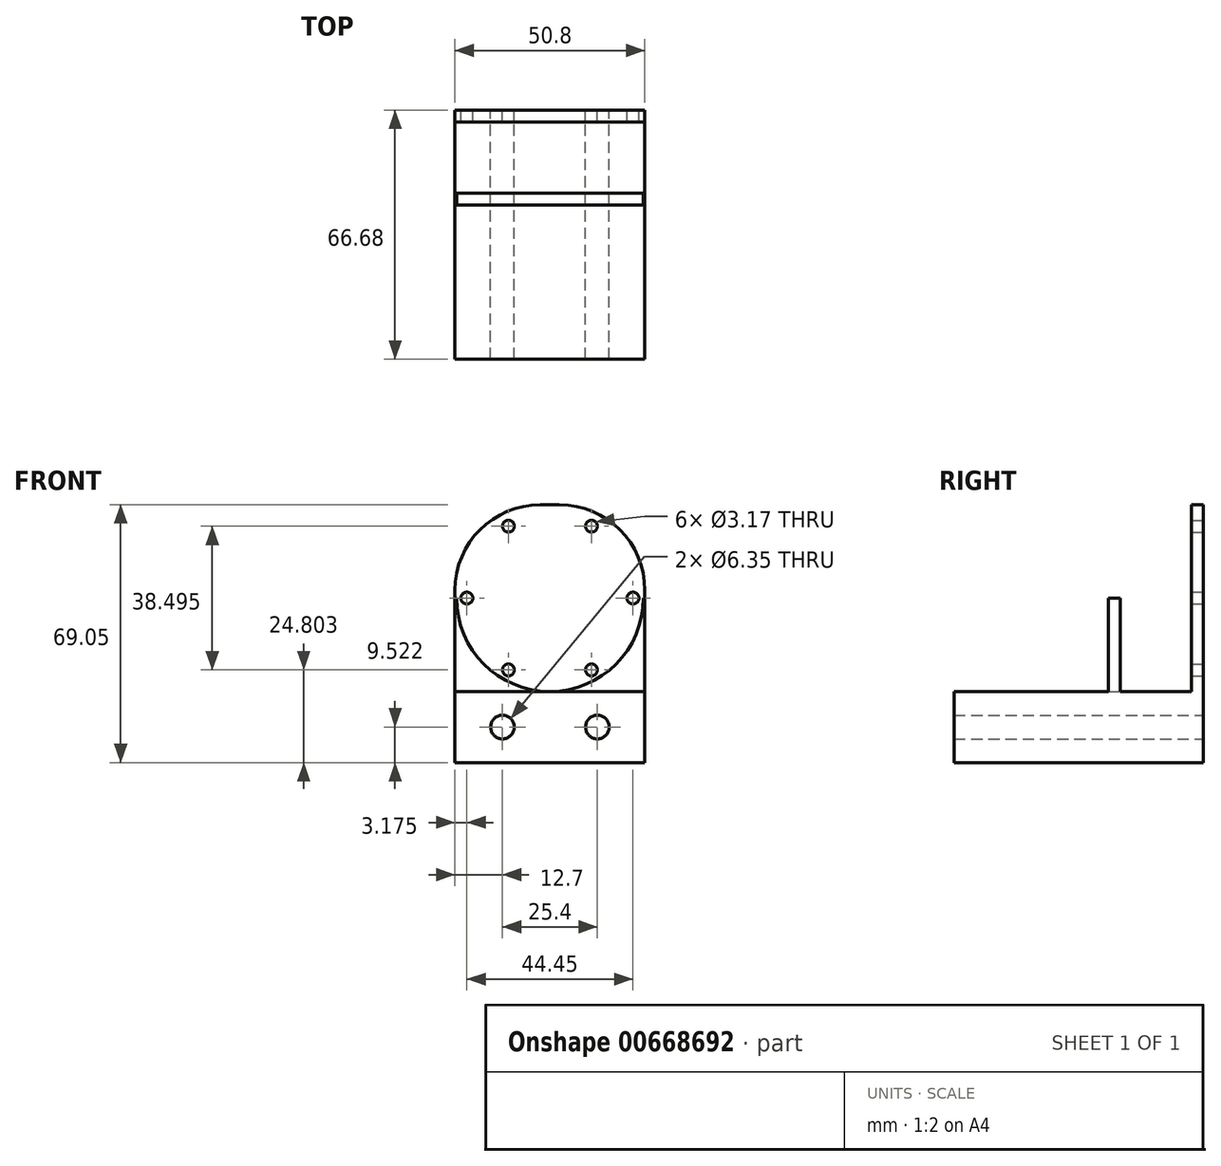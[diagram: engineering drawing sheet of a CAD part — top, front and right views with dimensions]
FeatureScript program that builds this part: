
annotation { "Feature Type Name" : "Feature", "Feature Type Description" : "" }
export const myFeature = defineFeature(function(context is Context, id is Id, definition is map)
    precondition{}
    {
        {
            var Q0;
            Q0=qCreatedBy(makeId("Front.planeOp"),FACE);
            var sketch = newSketch(context, id + "F0", { "sketchPlane" : qUnion([Q0])});
            skCircle(sketch, "E0", {"center": v(0, 0) * mm, "radius": 25 * mm});
            skCircle(sketch, "E1", {"center": v(0, 0) * mm, "radius": 23.81 * mm});
            skLineSegment(sketch, "E2", {"start": v(-23.81, 0) * mm, "end": v(-22.23, 0) * mm});
            skCircle(sketch, "E3", {"center": v(-22.23, 0) * mm, "radius": 1.59 * mm});
            skCircle(sketch, "E4.1.0", {"center": v(-11.11, -19.25) * mm, "radius": 1.59 * mm});
            skCircle(sketch, "E4.2.0", {"center": v(11.11, -19.25) * mm, "radius": 1.59 * mm});
            skCircle(sketch, "E4.3.0", {"center": v(22.23, 0) * mm, "radius": 1.59 * mm});
            skCircle(sketch, "E4.4.0", {"center": v(11.11, 19.25) * mm, "radius": 1.59 * mm});
            skCircle(sketch, "E4.5.0", {"center": v(-11.11, 19.25) * mm, "radius": 1.59 * mm});
            skLineSegment(sketch, "E5", {"start": v(0, -25) * mm, "end": v(-25.4, -25) * mm});
            skLineSegment(sketch, "E6", {"start": v(0, 25) * mm, "end": v(-25.4, 25) * mm});
            skLineSegment(sketch, "E7", {"start": v(-25.4, 25) * mm, "end": v(-25.4, -25) * mm});
            skLineSegment(sketch, "E8", {"start": v(0, -25) * mm, "end": v(25.4, -25) * mm});
            skLineSegment(sketch, "E9", {"start": v(0, 25) * mm, "end": v(25.4, 25) * mm});
            skLineSegment(sketch, "E10", {"start": v(25.4, 25) * mm, "end": v(25.4, -25) * mm});
            skLineSegment(sketch, "E11.bottom", {"start": v(-25.4, -25) * mm, "end": v(25.4, -25) * mm});
            skLineSegment(sketch, "E11.top", {"start": v(-25.4, -44.05) * mm, "end": v(25.4, -44.05) * mm});
            skLineSegment(sketch, "E11.left", {"start": v(-25.4, -25) * mm, "end": v(-25.4, -44.05) * mm});
            skLineSegment(sketch, "E11.right", {"start": v(25.4, -25) * mm, "end": v(25.4, -44.05) * mm});
            skLineSegment(sketch, "E12", {"start": v(-25.4, -34.53) * mm, "end": v(-12.7, -34.53) * mm});
            skCircle(sketch, "E13", {"center": v(-12.7, -34.53) * mm, "radius": 3.18 * mm});
            skCircle(sketch, "E14.MirrorC", {"center": v(12.7, -34.53) * mm, "radius": 3.18 * mm});
            skLineSegment(sketch, "E15", {"start": v(-23.81, 0) * mm, "end": v(-25.4, 0) * mm});
            skLineSegment(sketch, "E16", {"start": v(23.81, 0) * mm, "end": v(25.4, 0) * mm});
            skSolve(sketch);
        }
        {
            var Q0;
            {var subQ4=sQuery(id+"F0.wireOp",EDGE,"E11.top");Q0=makeQuery(id+"F0.imprint","IMPRINT",FACE,{"disambiguationData":[TD([[makeQuery(id+"F0.imprint","IMPRINT",EDGE,{"derivedFrom":subQ4}),1.0]])]});}
            extrude(context, id + "F1", {"entities" : qUnion([Q0]), "depth" : 66.67 * mm, "offsetDistance" : 25.4 * mm});
        }
        {
            var Q0;
            {var subQ0=sQuery(id+"F0.wireOp",EDGE,"E15");var subQ1=sQuery(id+"F0.wireOp",EDGE,"E0");var subQ2=makeQuery(id+"F0.imprint","INTERSECT",VERTEX,{"derivedFrom":[subQ1,subQ0]});Q0=makeQuery(id+"F0.imprint","IMPRINT",FACE,{"disambiguationData":[TD([[makeQuery(id+"F0.imprint","IMPRINT",EDGE,{"disambiguationData":[TD([[subQ2,-1.0]])],"derivedFrom":subQ1}),-1.0]])]});}
            var Q1;
            {var subQ0=sQuery(id+"F0.wireOp",EDGE,"E16");var subQ1=sQuery(id+"F0.wireOp",EDGE,"E0");var subQ2=makeQuery(id+"F0.imprint","INTERSECT",VERTEX,{"derivedFrom":[subQ1,subQ0]});Q1=makeQuery(id+"F0.imprint","IMPRINT",FACE,{"disambiguationData":[TD([[makeQuery(id+"F0.imprint","IMPRINT",EDGE,{"disambiguationData":[TD([[subQ2,1.0]])],"derivedFrom":subQ1}),-1.0]])]});}
            extrude(context, id + "F2", {"entities" : qUnion([Q0, Q1]), "operationType" : NewBodyOperationType.ADD, "depth" : 25.4 * mm, "offsetDistance" : 25.4 * mm});
        }
        {
            var Q0;
            {var subQ0=sQuery(id+"F0.wireOp",EDGE,"E15");var subQ1=sQuery(id+"F0.wireOp",EDGE,"E0");var subQ2=makeQuery(id+"F0.imprint","INTERSECT",VERTEX,{"derivedFrom":[subQ1,subQ0]});Q0=makeQuery(id+"F0.imprint","IMPRINT",FACE,{"disambiguationData":[TD([[makeQuery(id+"F0.imprint","IMPRINT",EDGE,{"disambiguationData":[TD([[subQ2,-1.0]])],"derivedFrom":subQ1}),-1.0]])]});}
            var Q1;
            {var subQ0=sQuery(id+"F0.wireOp",EDGE,"E16");var subQ1=sQuery(id+"F0.wireOp",EDGE,"E0");var subQ2=makeQuery(id+"F0.imprint","INTERSECT",VERTEX,{"derivedFrom":[subQ1,subQ0]});Q1=makeQuery(id+"F0.imprint","IMPRINT",FACE,{"disambiguationData":[TD([[makeQuery(id+"F0.imprint","IMPRINT",EDGE,{"disambiguationData":[TD([[subQ2,1.0]])],"derivedFrom":subQ1}),-1.0]])]});}
            extrude(context, id + "F3", {"entities" : qUnion([Q0, Q1]), "operationType" : NewBodyOperationType.REMOVE, "depth" : 22.22 * mm, "offsetDistance" : 25.4 * mm});
        }
        {
            var Q0;
            {var subQ3=sQuery(id+"F0.wireOp",EDGE,"E3");Q0=makeQuery(id+"F0.imprint","IMPRINT",FACE,{"disambiguationData":[TD([[makeQuery(id+"F0.imprint","IMPRINT",EDGE,{"derivedFrom":subQ3}),-1.0]])]});}
            var Q1;
            {var subQ1=sQuery(id+"F0.wireOp",EDGE,"E1");var subQ3=makeQuery(id+"F0.imprint","INTERSECT",VERTEX,{"derivedFrom":[subQ1,sQuery(id+"F0.wireOp",EDGE,"E4.4.0")]});Q1=makeQuery(id+"F0.imprint","IMPRINT",FACE,{"disambiguationData":[TD([[makeQuery(id+"F0.imprint","IMPRINT",EDGE,{"disambiguationData":[TD([[subQ3,-1.0]])],"derivedFrom":subQ1}),-1.0]])]});}
            var Q2;
            {var subQ0=sQuery(id+"F0.wireOp",EDGE,"E16");var subQ1=sQuery(id+"F0.wireOp",EDGE,"E0");var subQ2=makeQuery(id+"F0.imprint","INTERSECT",VERTEX,{"derivedFrom":[subQ1,subQ0]});Q2=makeQuery(id+"F0.imprint","IMPRINT",FACE,{"disambiguationData":[TD([[makeQuery(id+"F0.imprint","IMPRINT",EDGE,{"disambiguationData":[TD([[subQ2,1.0]])],"derivedFrom":subQ1}),-1.0]])]});}
            var Q3;
            {var subQ0=sQuery(id+"F0.wireOp",EDGE,"E15");var subQ1=sQuery(id+"F0.wireOp",EDGE,"E0");var subQ2=makeQuery(id+"F0.imprint","INTERSECT",VERTEX,{"derivedFrom":[subQ1,subQ0]});Q3=makeQuery(id+"F0.imprint","IMPRINT",FACE,{"disambiguationData":[TD([[makeQuery(id+"F0.imprint","IMPRINT",EDGE,{"disambiguationData":[TD([[subQ2,-1.0]])],"derivedFrom":subQ1}),-1.0]])]});}
            var Q4;
            {var subQ0=sQuery(id+"F0.wireOp",EDGE,"E9");Q4=makeQuery(id+"F0.imprint","IMPRINT",FACE,{"disambiguationData":[TD([[makeQuery(id+"F0.imprint","IMPRINT",EDGE,{"derivedFrom":subQ0}),-1.0]])]});}
            var Q5;
            {var subQ0=sQuery(id+"F0.wireOp",EDGE,"E6");Q5=makeQuery(id+"F0.imprint","IMPRINT",FACE,{"disambiguationData":[TD([[makeQuery(id+"F0.imprint","IMPRINT",EDGE,{"derivedFrom":subQ0}),1.0]])]});}
            var Q6;
            {var subQ3=sQuery(id+"F0.wireOp",EDGE,"E15");var subQ5=sQuery(id+"F0.wireOp",EDGE,"E0");var subQ6=makeQuery(id+"F0.imprint","INTERSECT",VERTEX,{"derivedFrom":[subQ5,subQ3]});Q6=makeQuery(id+"F0.imprint","IMPRINT",FACE,{"disambiguationData":[TD([[makeQuery(id+"F0.imprint","IMPRINT",EDGE,{"disambiguationData":[TD([[subQ6,-1.0]])],"derivedFrom":subQ5}),1.0]])]});}
            extrude(context, id + "F4", {"entities" : qUnion([Q0, Q1, Q2, Q3, Q4, Q5, Q6]), "operationType" : NewBodyOperationType.ADD, "depth" : 3.17 * mm, "offsetDistance" : 25.4 * mm});
        }
        {
            var Q0;
            Q0=makeQuery(id+"F4.opExtrude","SWEPT_EDGE",EDGE,{"disambiguationData":[OSD([sQuery(id+"F0.wireOp",EDGE,"E9"),sQuery(id+"F0.wireOp",EDGE,"E10")])]});
            var Q1;
            Q1=makeQuery(id+"F4.opExtrude","SWEPT_EDGE",EDGE,{"disambiguationData":[OSD([sQuery(id+"F0.wireOp",EDGE,"E6"),sQuery(id+"F0.wireOp",EDGE,"E7")])]});
            fillet(context, id + "F5", {"entities" : qUnion([Q0, Q1]), "radius" : 22.86 * mm, "tangentPropagation" : true, "allowEdgeOverflow" : false});
        }
    });
